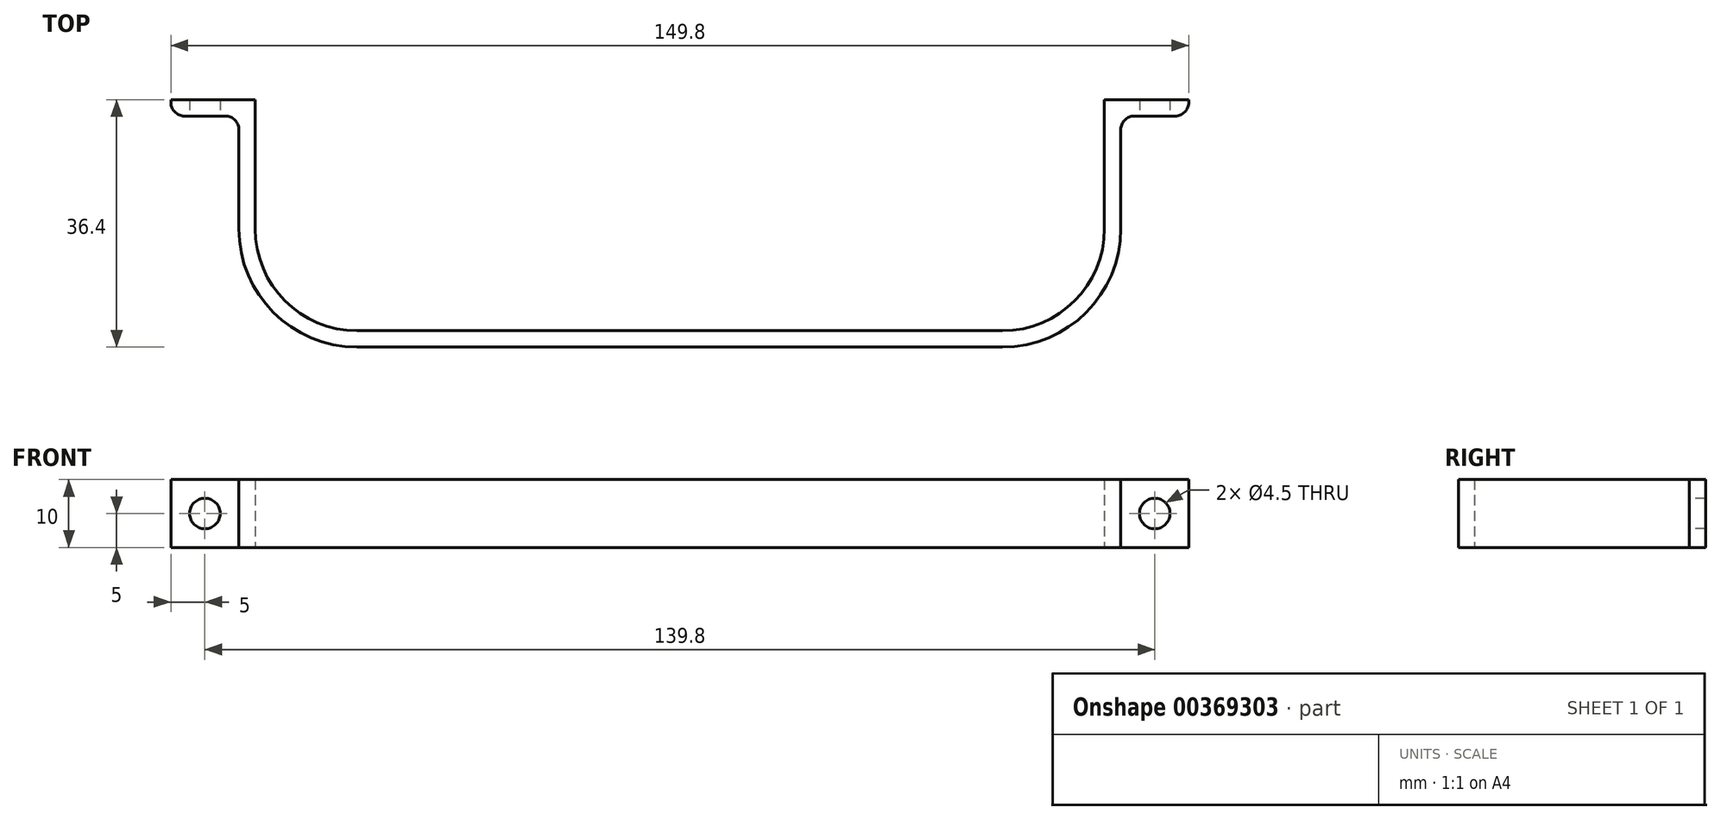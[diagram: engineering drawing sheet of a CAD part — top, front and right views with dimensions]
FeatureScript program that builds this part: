
annotation { "Feature Type Name" : "Feature", "Feature Type Description" : "" }
export const myFeature = defineFeature(function(context is Context, id is Id, definition is map)
    precondition{}
    {
        {
            var Q0;
            Q0=qCreatedBy(makeId("Top.planeOp"),FACE);
            var sketch = newSketch(context, id + "F0", { "sketchPlane" : qUnion([Q0])});
            skLineSegment(sketch, "E0", {"start": v(0, 0) * mm, "end": v(47.5, 0) * mm});
            skLineSegment(sketch, "E1", {"start": v(0, 0) * mm, "end": v(0, 2.4) * mm});
            skLineSegment(sketch, "E2", {"start": v(0, 2.4) * mm, "end": v(47.5, 2.4) * mm});
            skArc(sketch, "E3", {"start": v(47.5, 2.4) * mm, "mid": v(58.1, 6.8) * mm, "end": v(62.5, 17.4) * mm});
            skArc(sketch, "E4", {"start": v(47.5, 0) * mm, "mid": v(59.8, 5.1) * mm, "end": v(64.9, 17.4) * mm});
            skLineSegment(sketch, "E5", {"start": v(64.9, 17.4) * mm, "end": v(64.9, 34) * mm});
            skLineSegment(sketch, "E6", {"start": v(64.9, 34) * mm, "end": v(74.9, 34) * mm});
            skLineSegment(sketch, "E7", {"start": v(74.9, 34) * mm, "end": v(74.9, 36.4) * mm});
            skLineSegment(sketch, "E8", {"start": v(74.9, 36.4) * mm, "end": v(62.5, 36.4) * mm});
            skLineSegment(sketch, "E9", {"start": v(62.5, 36.4) * mm, "end": v(62.5, 17.4) * mm});
            skSolve(sketch);
        }
        {
            var Q0;
            Q0 = qSketchRegion(id + "F0", true);
            extrude(context, id + "F1", {"entities" : qUnion([Q0]), "endBound" : BoundingType.SYMMETRIC, "depth" : 10 * mm});
        }
        {
            var Q0;
            Q0=makeQuery(id+"F1.opExtrude","SWEPT_FACE",FACE,{"disambiguationData":[OSD([sQuery(id+"F0.wireOp",EDGE,"E6")])]});
            var sketch = newSketch(context, id + "F2", { "sketchPlane" : qUnion([Q0])});
            skPoint(sketch, "E10", {"position": v(69.9, 0) * mm});
            skPoint(sketch, "E10.positionSnap0", {"position": v(69.9, 5) * mm});
            skSolve(sketch);
        }
        {
            var Q0;
            Q0=sQuery(id+"F2.wireOp",VERTEX,"E10");
            var Q1;
            Q1=makeQuery(id+"F1.opExtrude","SWEPT_BODY",BODY,{"disambiguationData":[OSD([sQuery(id+"F0.wireOp",EDGE,"E0"),sQuery(id+"F0.wireOp",EDGE,"E1"),sQuery(id+"F0.wireOp",EDGE,"E2"),sQuery(id+"F0.wireOp",EDGE,"E3"),sQuery(id+"F0.wireOp",EDGE,"E4"),sQuery(id+"F0.wireOp",EDGE,"E5"),sQuery(id+"F0.wireOp",EDGE,"E6"),sQuery(id+"F0.wireOp",EDGE,"E7"),sQuery(id+"F0.wireOp",EDGE,"E8"),sQuery(id+"F0.wireOp",EDGE,"E9")])]});
            hole(context, id + "F3", {"style" : HoleStyle.SIMPLE, "endStyle" : HoleEndStyle.THROUGH, "standardTappedOrClearance" : lookupTablePath({ "standard" : "ANSI", "fit" : "Normal (ASME)", "size" : "#8", "type" : "Clearance" }), "standardBlindInLast" : lookupTablePath({ "fit" : "Free", "standard" : "ANSI", "size" : "#8", "type" : "Clearance" }), "holeDiameter" : 4.5 * mm, "isTappedThrough" : true, "tappedDepth" : 12 * mm, "tapClearance" : 3, "locations" : qUnion([Q0]), "scope" : qUnion([Q1])});
        }
        {
            var Q0;
            Q0=makeQuery(id+"F1.opExtrude","SWEPT_EDGE",EDGE,{"disambiguationData":[OSD([sQuery(id+"F0.wireOp",EDGE,"E5"),sQuery(id+"F0.wireOp",EDGE,"E6")])]});
            var Q1;
            Q1=makeQuery(id+"F1.opExtrude","SWEPT_EDGE",EDGE,{"disambiguationData":[OSD([sQuery(id+"F0.wireOp",EDGE,"E6"),sQuery(id+"F0.wireOp",EDGE,"E7")])]});
            fillet(context, id + "F4", {"entities" : qUnion([Q0, Q1]), "radius" : 2 * mm, "tangentPropagation" : true, "allowEdgeOverflow" : false});
        }
        {
            var Q0;
            Q0=makeQuery(id+"F1.opExtrude","SWEPT_BODY",BODY,{"disambiguationData":[OSD([sQuery(id+"F0.wireOp",EDGE,"E0"),sQuery(id+"F0.wireOp",EDGE,"E1"),sQuery(id+"F0.wireOp",EDGE,"E2"),sQuery(id+"F0.wireOp",EDGE,"E3"),sQuery(id+"F0.wireOp",EDGE,"E4"),sQuery(id+"F0.wireOp",EDGE,"E5"),sQuery(id+"F0.wireOp",EDGE,"E6"),sQuery(id+"F0.wireOp",EDGE,"E7"),sQuery(id+"F0.wireOp",EDGE,"E8"),sQuery(id+"F0.wireOp",EDGE,"E9")])]});
            var Q1;
            Q1=makeQuery(id+"F1.opExtrude","SWEPT_FACE",FACE,{"disambiguationData":[OSD([sQuery(id+"F0.wireOp",EDGE,"E1")])]});
            mirror(context, id + "F5", {"operationType" : NewBodyOperationType.ADD, "entities" : qUnion([Q0]), "mirrorPlane" : qUnion([Q1])});
        }
    });
